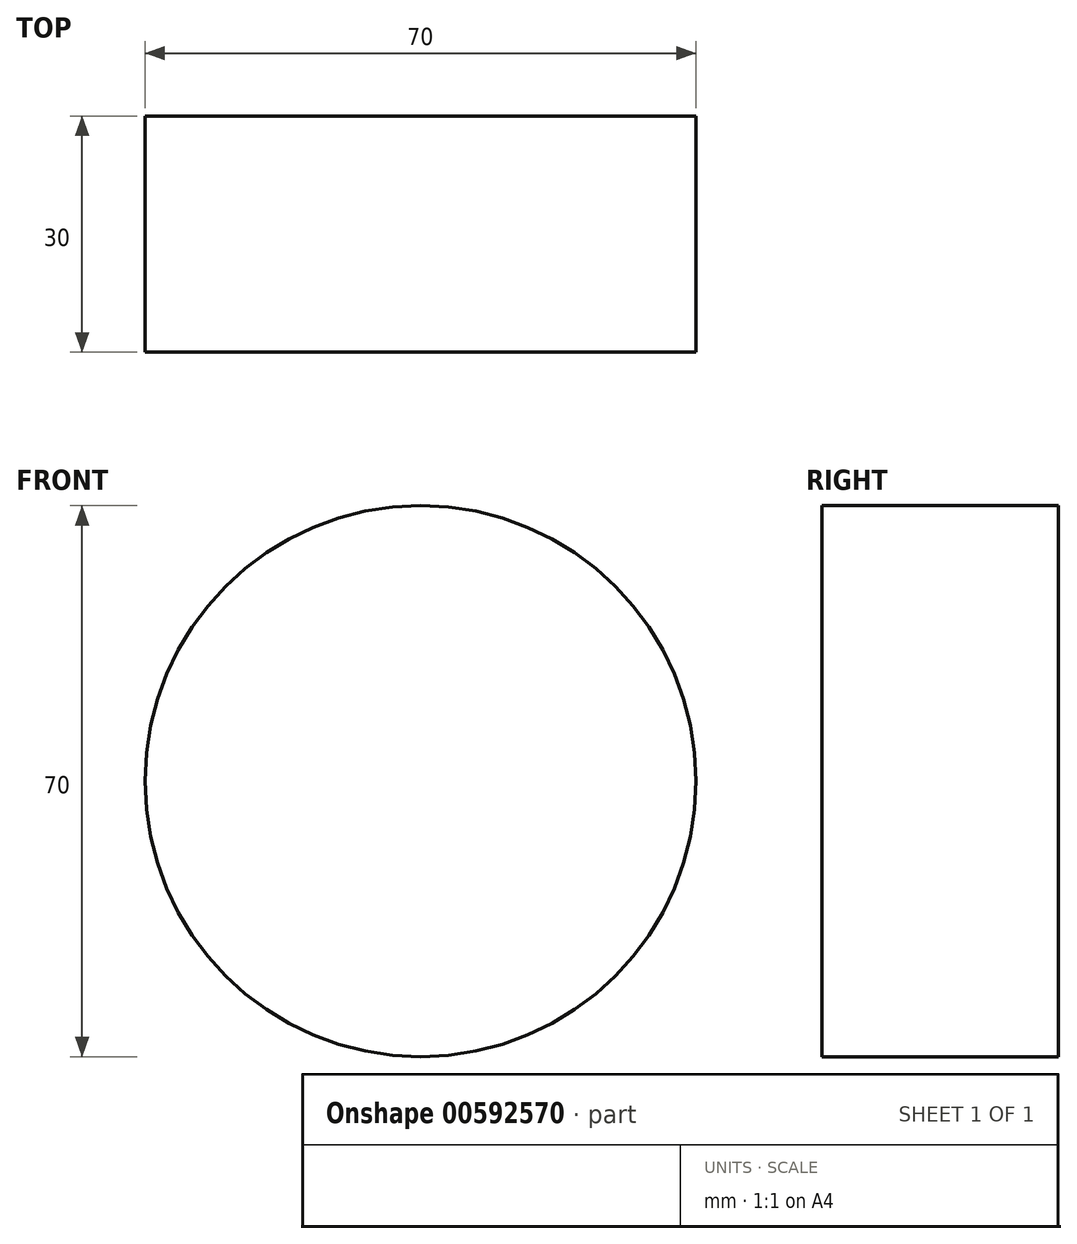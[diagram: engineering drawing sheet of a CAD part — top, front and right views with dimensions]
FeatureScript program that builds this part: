
annotation { "Feature Type Name" : "Feature", "Feature Type Description" : "" }
export const myFeature = defineFeature(function(context is Context, id is Id, definition is map)
    precondition{}
    {
        {
            var Q0;
            Q0=qCreatedBy(makeId("Front.planeOp"),FACE);
            var sketch = newSketch(context, id + "F0", { "sketchPlane" : qUnion([Q0])});
            skCircle(sketch, "E0", {"center": v(0, 0) * mm, "radius": 35 * mm});
            skSolve(sketch);
        }
        {
            var Q0;
            Q0 = qSketchRegion(id + "F0", true);
            extrude(context, id + "F1", {"entities" : qUnion([Q0]), "depth" : 30 * mm, "offsetDistance" : 25.4 * mm});
        }
    });
